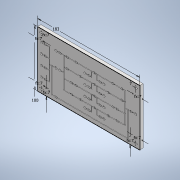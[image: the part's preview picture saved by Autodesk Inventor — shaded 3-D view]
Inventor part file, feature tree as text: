
AUTODESK INVENTOR PART (.ipt)
format: ipt  version: 2021 (Build 250183000, 183)  size: 758,272 bytes
history: native  units: in
note: dims shown in document units (in); Inventor stores cm internally (conversion verified against a paired STEP export)
features: other x9, extrude x4, hole x2, surface_op x1
ambient origin geometry x8: Origin, YZ Plane, XZ Plane, XY Plane, X Axis, Y Axis, Z Axis, Center Point
bodies: Solid1 (feature_tree)
feature tree (16):
  other  "points for corner holes"
  extrude  "Extrusion base plate"  Depth=6.6929in
  other  "plane above base plate to create rib"
  other  "channels and points for valves and for connectors"
  other  "channels as rib"
  extrude  "extrusion of rib to get cutout"  Depth=8.6614in
  other  "valve shape"
  extrude  "valve space extrusion"  Depth=0.1969in
  extrude  "valve bar extrusion"  Depth=0.3543in
  other  "all valve spaces"
  other  "projected point for every hole"
  hole  "holes for connectors"  [1 undecoded]
  hole  "holes in corners"  [1 undecoded]
  other  "valve bar shape"
  other  "Projected points for every valve"
  surface_op  "surface of rib as sketch"
note: 2 required parameter values undecoded (feature->parameter linkage not recoverable at this tier; creation-order binding heuristic only, values carry confidence <= 0.55)
